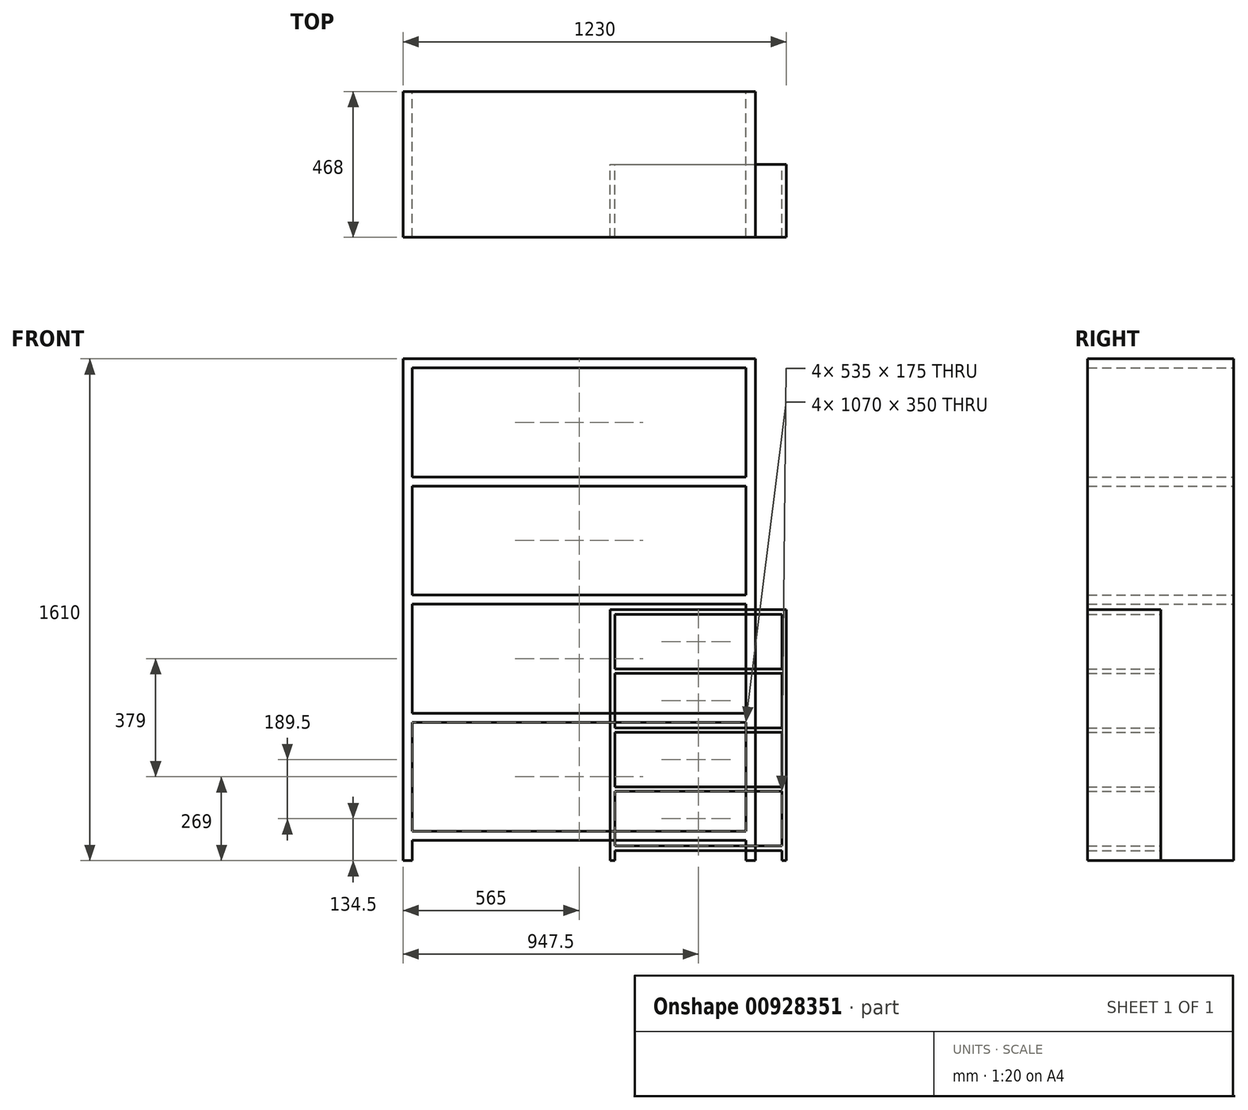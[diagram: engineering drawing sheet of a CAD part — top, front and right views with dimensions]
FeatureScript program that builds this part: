
annotation { "Feature Type Name" : "Feature", "Feature Type Description" : "" }
export const myFeature = defineFeature(function(context is Context, id is Id, definition is map)
    precondition{}
    {
        {
            var Q0;
            Q0=qCreatedBy(makeId("Front.planeOp"),FACE);
            var sketch = newSketch(context, id + "F0", { "sketchPlane" : qUnion([Q0])});
            skLineSegment(sketch, "E0.bottom", {"start": v(0, 0) * mm, "end": v(1130, 0) * mm});
            skLineSegment(sketch, "E0.top", {"start": v(0, 1610) * mm, "end": v(1130, 1610) * mm});
            skLineSegment(sketch, "E0.left", {"start": v(0, 0) * mm, "end": v(0, 1610) * mm});
            skLineSegment(sketch, "E0.right", {"start": v(1130, 0) * mm, "end": v(1130, 1610) * mm});
            skLineSegment(sketch, "E1", {"start": v(565, 1610) * mm, "end": v(565, 0) * mm, "construction": true});
            skLineSegment(sketch, "E2.bottom", {"start": v(30, 1231) * mm, "end": v(1100, 1231) * mm});
            skLineSegment(sketch, "E2.top", {"start": v(30, 1581) * mm, "end": v(1100, 1581) * mm});
            skLineSegment(sketch, "E2.left", {"start": v(30, 1231) * mm, "end": v(30, 1581) * mm});
            skLineSegment(sketch, "E2.right", {"start": v(1100, 1231) * mm, "end": v(1100, 1581) * mm});
            skPoint(sketch, "E2.middle", {"position": v(565, 1406) * mm});
            skLineSegment(sketch, "E3.0.1.0", {"start": v(30, 1202) * mm, "end": v(1100, 1202) * mm});
            skLineSegment(sketch, "E3.0.1.1", {"start": v(30, 852) * mm, "end": v(30, 1202) * mm});
            skLineSegment(sketch, "E3.0.1.2", {"start": v(30, 852) * mm, "end": v(1100, 852) * mm});
            skLineSegment(sketch, "E3.0.1.3", {"start": v(1100, 852) * mm, "end": v(1100, 1202) * mm});
            skLineSegment(sketch, "E3.0.2.0", {"start": v(30, 823) * mm, "end": v(1100, 823) * mm});
            skLineSegment(sketch, "E3.0.2.1", {"start": v(30, 473) * mm, "end": v(30, 823) * mm});
            skLineSegment(sketch, "E3.0.2.2", {"start": v(30, 473) * mm, "end": v(1100, 473) * mm});
            skLineSegment(sketch, "E3.0.2.3", {"start": v(1100, 473) * mm, "end": v(1100, 823) * mm});
            skLineSegment(sketch, "E3.0.3.0", {"start": v(30, 444) * mm, "end": v(1100, 444) * mm});
            skLineSegment(sketch, "E3.0.3.1", {"start": v(30, 94) * mm, "end": v(30, 444) * mm});
            skLineSegment(sketch, "E3.0.3.2", {"start": v(30, 94) * mm, "end": v(1100, 94) * mm});
            skLineSegment(sketch, "E3.0.3.3", {"start": v(1100, 94) * mm, "end": v(1100, 444) * mm});
            skLineSegment(sketch, "E3.direction1", {"start": v(30, 1231) * mm, "end": v(1160, 1231) * mm, "construction": true});
            skLineSegment(sketch, "E3.direction2", {"start": v(30, 1231) * mm, "end": v(30, 852) * mm, "construction": true});
            skLineSegment(sketch, "E4", {"start": v(1100, 65) * mm, "end": v(30, 65) * mm});
            skLineSegment(sketch, "E5", {"start": v(30, 65) * mm, "end": v(30, 0) * mm});
            skLineSegment(sketch, "E6.MirrorCS", {"start": v(1100, 65) * mm, "end": v(1100, 0) * mm});
            skSolve(sketch);
        }
        {
            var Q0;
            Q0=makeQuery(id+"F0.imprint","IMPRINT",FACE,{"disambiguationData":[TD([[makeQuery(id+"F0.imprint","IMPRINT",EDGE,{"derivedFrom":sQuery(id+"F0.wireOp",EDGE,"E0.bottom")}),1.0]])]});
            extrude(context, id + "F1", {"entities" : qUnion([Q0]), "depth" : 468 * mm, "offsetDistance" : 25 * mm});
        }
        {
            var Q0;
            Q0=makeQuery(id+"F1.opExtrude","SWEPT_BODY",BODY,{"disambiguationData":[OSD([sQuery(id+"F0.wireOp",EDGE,"E0.bottom"),sQuery(id+"F0.wireOp",EDGE,"E0.top"),sQuery(id+"F0.wireOp",EDGE,"E0.left"),sQuery(id+"F0.wireOp",EDGE,"E0.right"),sQuery(id+"F0.wireOp",EDGE,"E2.bottom"),sQuery(id+"F0.wireOp",EDGE,"E2.top"),sQuery(id+"F0.wireOp",EDGE,"E2.left"),sQuery(id+"F0.wireOp",EDGE,"E2.right"),sQuery(id+"F0.wireOp",EDGE,"E3.0.1.0"),sQuery(id+"F0.wireOp",EDGE,"E3.0.1.1"),sQuery(id+"F0.wireOp",EDGE,"E3.0.1.2"),sQuery(id+"F0.wireOp",EDGE,"E3.0.1.3"),sQuery(id+"F0.wireOp",EDGE,"E3.0.2.0"),sQuery(id+"F0.wireOp",EDGE,"E3.0.2.1"),sQuery(id+"F0.wireOp",EDGE,"E3.0.2.2"),sQuery(id+"F0.wireOp",EDGE,"E3.0.2.3"),sQuery(id+"F0.wireOp",EDGE,"E3.0.3.0"),sQuery(id+"F0.wireOp",EDGE,"E3.0.3.1"),sQuery(id+"F0.wireOp",EDGE,"E3.0.3.2"),sQuery(id+"F0.wireOp",EDGE,"E3.0.3.3"),sQuery(id+"F0.wireOp",EDGE,"E4"),sQuery(id+"F0.wireOp",EDGE,"E5"),sQuery(id+"F0.wireOp",EDGE,"E6.MirrorCS")])]});
            var Q1;
            Q1=makeQuery(id+"F1.opExtrude","CAP_VERTEX",VERTEX,{"disambiguationData":[OSD([sQuery(id+"F0.wireOp",EDGE,"E0.bottom"),sQuery(id+"F0.wireOp",EDGE,"E0.right")])],"isStart":false});
            transform(context, id + "F2", {"entities" : qUnion([Q0]), "transformType" : TransformType.SCALE_UNIFORMLY, "scale" : .5, "scalePoint" : qUnion([Q1]), "makeCopy" : true});
        }
        {
            var Q0;
            Q0=makeQuery(id+"F2.opPattern","COPY",BODY,{"derivedFrom":makeQuery(id+"F1.opExtrude","SWEPT_BODY",BODY,{"disambiguationData":[OSD([sQuery(id+"F0.wireOp",EDGE,"E0.bottom"),sQuery(id+"F0.wireOp",EDGE,"E0.top"),sQuery(id+"F0.wireOp",EDGE,"E0.left"),sQuery(id+"F0.wireOp",EDGE,"E0.right"),sQuery(id+"F0.wireOp",EDGE,"E2.bottom"),sQuery(id+"F0.wireOp",EDGE,"E2.top"),sQuery(id+"F0.wireOp",EDGE,"E2.left"),sQuery(id+"F0.wireOp",EDGE,"E2.right"),sQuery(id+"F0.wireOp",EDGE,"E3.0.1.0"),sQuery(id+"F0.wireOp",EDGE,"E3.0.1.1"),sQuery(id+"F0.wireOp",EDGE,"E3.0.1.2"),sQuery(id+"F0.wireOp",EDGE,"E3.0.1.3"),sQuery(id+"F0.wireOp",EDGE,"E3.0.2.0"),sQuery(id+"F0.wireOp",EDGE,"E3.0.2.1"),sQuery(id+"F0.wireOp",EDGE,"E3.0.2.2"),sQuery(id+"F0.wireOp",EDGE,"E3.0.2.3"),sQuery(id+"F0.wireOp",EDGE,"E3.0.3.0"),sQuery(id+"F0.wireOp",EDGE,"E3.0.3.1"),sQuery(id+"F0.wireOp",EDGE,"E3.0.3.2"),sQuery(id+"F0.wireOp",EDGE,"E3.0.3.3"),sQuery(id+"F0.wireOp",EDGE,"E4"),sQuery(id+"F0.wireOp",EDGE,"E5"),sQuery(id+"F0.wireOp",EDGE,"E6.MirrorCS")])]}),"instanceName":"1"});
            transform(context, id + "F3", {"entities" : qUnion([Q0]), "transformType" : TransformType.TRANSLATION_3D, "dx" : 100 * mm, "dy" : 0 * mm, "dz" : 0 * mm, "makeCopy" : false});
        }
    });
